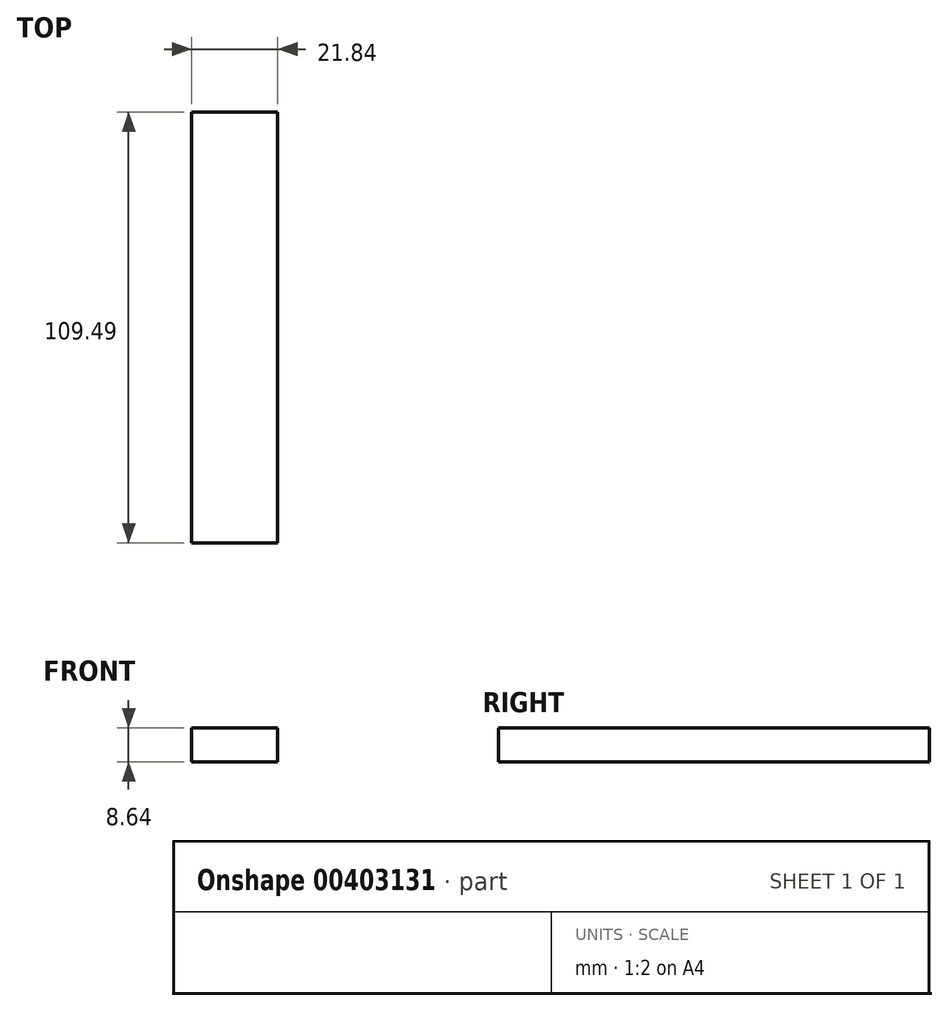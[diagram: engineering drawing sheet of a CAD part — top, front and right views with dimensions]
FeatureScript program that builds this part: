
annotation { "Feature Type Name" : "Feature", "Feature Type Description" : "" }
export const myFeature = defineFeature(function(context is Context, id is Id, definition is map)
    precondition{}
    {
        {
            var Q0;
            Q0=qCreatedBy(makeId("Top.planeOp"),FACE);
            var sketch = newSketch(context, id + "F0", { "sketchPlane" : qUnion([Q0])});
            skLineSegment(sketch, "E0.bottom", {"start": v(-10.92, 0) * mm, "end": v(10.92, 0) * mm});
            skLineSegment(sketch, "E0.top", {"start": v(-10.92, -109.5) * mm, "end": v(10.92, -109.5) * mm});
            skLineSegment(sketch, "E0.left", {"start": v(-10.92, 0) * mm, "end": v(-10.92, -109.5) * mm});
            skLineSegment(sketch, "E0.right", {"start": v(10.92, 0) * mm, "end": v(10.92, -109.5) * mm});
            skPoint(sketch, "E0.middle", {"position": v(0, -54.75) * mm});
            skSolve(sketch);
        }
        {
            var Q0;
            Q0 = qSketchRegion(id + "F0", true);
            extrude(context, id + "F1", {"entities" : qUnion([Q0]), "depth" : 8.64 * mm});
        }
        {
            var Q0;
            Q0=qCreatedBy(makeId("Top.planeOp"),FACE);
            var sketch = newSketch(context, id + "F2", { "sketchPlane" : qUnion([Q0])});
            skCircle(sketch, "E1", {"center": v(0, -126.87) * mm, "radius": 22.85 * mm});
            skSolve(sketch);
        }
        {
            var Q0;
            Q0 = qSketchRegion(id + "F2", true);
            var Q1;
            Q1=sQuery(id+"F2.wireOp",EDGE,"E1");
            extrude(context, id + "F3", {"entities" : qUnion([Q0]), "bodyType" : ToolBodyType.SURFACE, "surfaceEntities" : qUnion([Q1]), "depth" : 7.5 * mm});
        }
    });
